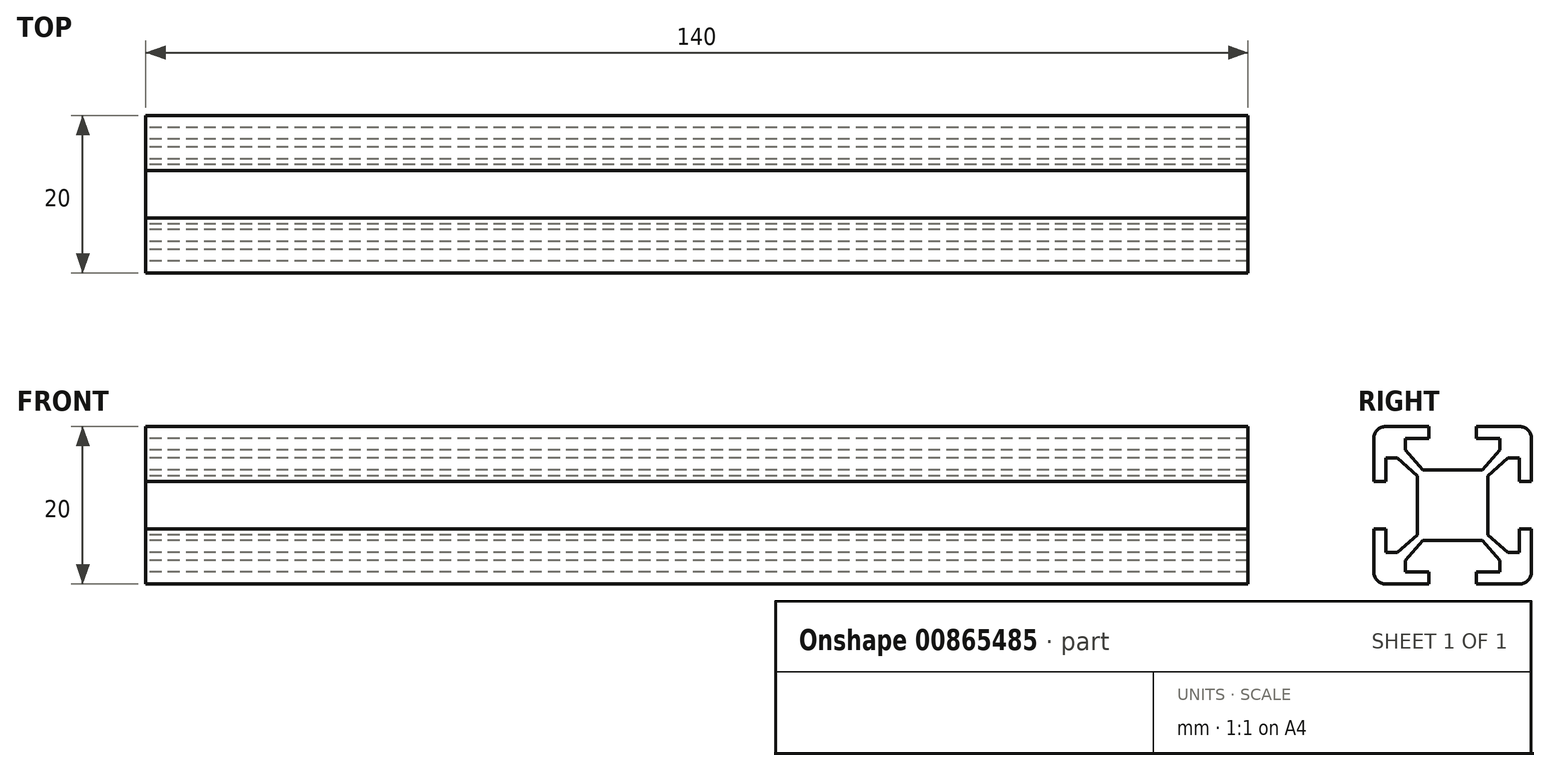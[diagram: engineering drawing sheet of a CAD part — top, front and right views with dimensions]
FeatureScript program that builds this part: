
annotation { "Feature Type Name" : "Feature", "Feature Type Description" : "" }
export const myFeature = defineFeature(function(context is Context, id is Id, definition is map)
    precondition{}
    {
        {
            var Q0;
            Q0=qCreatedBy(makeId("Right.planeOp"),FACE);
            var sketch = newSketch(context, id + "F0", { "sketchPlane" : qUnion([Q0])});
            skLineSegment(sketch, "E0.bottom", {"start": v(8.5, 10) * mm, "end": v(3, 10) * mm});
            skLineSegment(sketch, "E0.top", {"start": v(8.5, -10) * mm, "end": v(-8.5, -10) * mm});
            skLineSegment(sketch, "E0.left", {"start": v(10, 8.5) * mm, "end": v(10, 3) * mm});
            skLineSegment(sketch, "E0.right", {"start": v(-10, 8.5) * mm, "end": v(-10, 3) * mm});
            skPoint(sketch, "E0.middle", {"position": v(0, 0) * mm});
            skPoint(sketch, "E1.visualSharp", {"position": v(-10, 10) * mm});
            skArc(sketch, "E1.filletArc", {"start": v(-8.5, 10) * mm, "mid": v(-9.56, 9.56) * mm, "end": v(-10, 8.5) * mm});
            skPoint(sketch, "E2.visualSharp", {"position": v(10, 10) * mm});
            skArc(sketch, "E2.filletArc", {"start": v(10, 8.5) * mm, "mid": v(9.56, 9.56) * mm, "end": v(8.5, 10) * mm});
            skPoint(sketch, "E3.visualSharp", {"position": v(10, -10) * mm});
            skArc(sketch, "E3.filletArc", {"start": v(8.5, -10) * mm, "mid": v(9.56, -9.56) * mm, "end": v(10, -8.5) * mm});
            skPoint(sketch, "E4.visualSharp", {"position": v(-10, -10) * mm});
            skArc(sketch, "E4.filletArc", {"start": v(-10, -8.5) * mm, "mid": v(-9.56, -9.56) * mm, "end": v(-8.5, -10) * mm});
            skLineSegment(sketch, "E5", {"start": v(-3, 10) * mm, "end": v(-3, 8.5) * mm});
            skLineSegment(sketch, "E6", {"start": v(-3, 8.5) * mm, "end": v(-6, 8.5) * mm});
            skLineSegment(sketch, "E7", {"start": v(-6, 8.5) * mm, "end": v(-6, 7) * mm});
            skLineSegment(sketch, "E8", {"start": v(-6, 7) * mm, "end": v(-3.75, 4.5) * mm});
            skLineSegment(sketch, "E9", {"start": v(-3.75, 4.5) * mm, "end": v(0, 4.5) * mm});
            skLineSegment(sketch, "E10.MirrorCS", {"start": v(3, 10) * mm, "end": v(3, 8.5) * mm});
            skLineSegment(sketch, "E11.MirrorCS", {"start": v(3, 8.5) * mm, "end": v(6, 8.5) * mm});
            skLineSegment(sketch, "E12.MirrorCS", {"start": v(6, 8.5) * mm, "end": v(6, 7) * mm});
            skLineSegment(sketch, "E13.MirrorCS", {"start": v(6, 7) * mm, "end": v(3.75, 4.5) * mm});
            skLineSegment(sketch, "E14.MirrorCS", {"start": v(3.75, 4.5) * mm, "end": v(0, 4.5) * mm});
            skLineSegment(sketch, "E15.trimOffspring", {"start": v(-3, 10) * mm, "end": v(-8.5, 10) * mm});
            skLineSegment(sketch, "E16.1.0", {"start": v(-8.5, -3) * mm, "end": v(-8.5, -6) * mm});
            skLineSegment(sketch, "E16.1.1", {"start": v(-8.5, -6) * mm, "end": v(-7, -6) * mm});
            skLineSegment(sketch, "E16.1.2", {"start": v(-7, -6) * mm, "end": v(-4.5, -3.75) * mm});
            skLineSegment(sketch, "E16.1.3", {"start": v(-4.5, -3.75) * mm, "end": v(-4.5, 0) * mm});
            skLineSegment(sketch, "E16.1.4", {"start": v(-4.5, 3.75) * mm, "end": v(-4.5, 0) * mm});
            skLineSegment(sketch, "E16.1.5", {"start": v(-7, 6) * mm, "end": v(-4.5, 3.75) * mm});
            skLineSegment(sketch, "E16.1.6", {"start": v(-8.5, 6) * mm, "end": v(-7, 6) * mm});
            skLineSegment(sketch, "E16.1.7", {"start": v(-8.5, 3) * mm, "end": v(-8.5, 6) * mm});
            skLineSegment(sketch, "E16.1.8", {"start": v(-10, 3) * mm, "end": v(-8.5, 3) * mm});
            skLineSegment(sketch, "E16.1.9", {"start": v(-10, -3) * mm, "end": v(-8.5, -3) * mm});
            skLineSegment(sketch, "E16.2.0", {"start": v(3, -8.5) * mm, "end": v(6, -8.5) * mm});
            skLineSegment(sketch, "E16.2.1", {"start": v(6, -8.5) * mm, "end": v(6, -7) * mm});
            skLineSegment(sketch, "E16.2.2", {"start": v(6, -7) * mm, "end": v(3.75, -4.5) * mm});
            skLineSegment(sketch, "E16.2.3", {"start": v(3.75, -4.5) * mm, "end": v(0, -4.5) * mm});
            skLineSegment(sketch, "E16.2.4", {"start": v(-3.75, -4.5) * mm, "end": v(0, -4.5) * mm});
            skLineSegment(sketch, "E16.2.5", {"start": v(-6, -7) * mm, "end": v(-3.75, -4.5) * mm});
            skLineSegment(sketch, "E16.2.6", {"start": v(-6, -8.5) * mm, "end": v(-6, -7) * mm});
            skLineSegment(sketch, "E16.2.7", {"start": v(-3, -8.5) * mm, "end": v(-6, -8.5) * mm});
            skLineSegment(sketch, "E16.2.8", {"start": v(-3, -10) * mm, "end": v(-3, -8.5) * mm});
            skLineSegment(sketch, "E16.2.9", {"start": v(3, -10) * mm, "end": v(3, -8.5) * mm});
            skLineSegment(sketch, "E16.3.0", {"start": v(8.5, 3) * mm, "end": v(8.5, 6) * mm});
            skLineSegment(sketch, "E16.3.1", {"start": v(8.5, 6) * mm, "end": v(7, 6) * mm});
            skLineSegment(sketch, "E16.3.2", {"start": v(7, 6) * mm, "end": v(4.5, 3.75) * mm});
            skLineSegment(sketch, "E16.3.3", {"start": v(4.5, 3.75) * mm, "end": v(4.5, 0) * mm});
            skLineSegment(sketch, "E16.3.4", {"start": v(4.5, -3.75) * mm, "end": v(4.5, 0) * mm});
            skLineSegment(sketch, "E16.3.5", {"start": v(7, -6) * mm, "end": v(4.5, -3.75) * mm});
            skLineSegment(sketch, "E16.3.6", {"start": v(8.5, -6) * mm, "end": v(7, -6) * mm});
            skLineSegment(sketch, "E16.3.7", {"start": v(8.5, -3) * mm, "end": v(8.5, -6) * mm});
            skLineSegment(sketch, "E16.3.8", {"start": v(10, -3) * mm, "end": v(8.5, -3) * mm});
            skLineSegment(sketch, "E16.3.9", {"start": v(10, 3) * mm, "end": v(8.5, 3) * mm});
            skLineSegment(sketch, "E17.trimOffspring", {"start": v(-10, -3) * mm, "end": v(-10, -8.5) * mm});
            skLineSegment(sketch, "E18.trimOffspring", {"start": v(10, -3) * mm, "end": v(10, -8.5) * mm});
            skSolve(sketch);
        }
        {
            var Q0;
            Q0=makeQuery(id+"F0.imprint","IMPRINT",FACE,{"disambiguationData":[TD([[makeQuery(id+"F0.imprint","IMPRINT",EDGE,{"derivedFrom":sQuery(id+"F0.wireOp",EDGE,"E0.bottom")}),1.0]])]});
            extrude(context, id + "F1", {"entities" : qUnion([Q0]), "depth" : 140 * mm, "offsetDistance" : 25 * mm});
        }
    });
